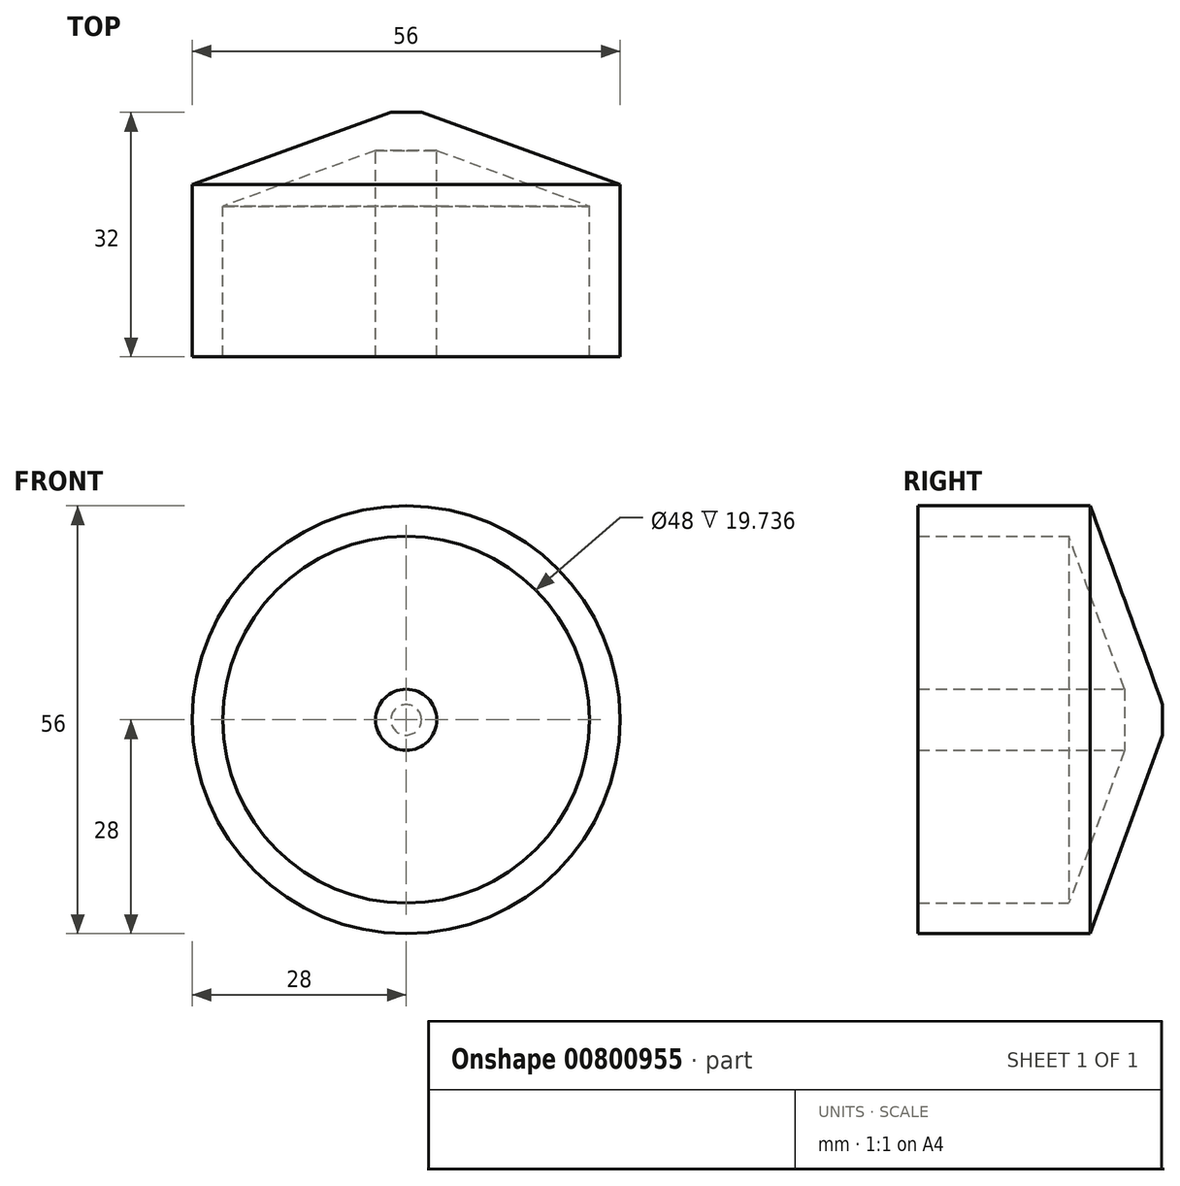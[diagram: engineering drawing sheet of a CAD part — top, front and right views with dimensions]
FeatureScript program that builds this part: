
annotation { "Feature Type Name" : "Feature", "Feature Type Description" : "" }
export const myFeature = defineFeature(function(context is Context, id is Id, definition is map)
    precondition{}
    {
        {
            var Q0;
            Q0=qCreatedBy(makeId("Top.planeOp"),FACE);
            var sketch = newSketch(context, id + "F0", { "sketchPlane" : qUnion([Q0])});
            skLineSegment(sketch, "E0", {"start": v(0, 0) * mm, "end": v(0, -32) * mm});
            skLineSegment(sketch, "E1", {"start": v(0, -32) * mm, "end": v(4, -32) * mm});
            skLineSegment(sketch, "E2", {"start": v(4, -32) * mm, "end": v(4, -4.98) * mm});
            skLineSegment(sketch, "E3", {"start": v(4, -4.98) * mm, "end": v(24, -12.26) * mm});
            skLineSegment(sketch, "E4", {"start": v(24, -12.26) * mm, "end": v(24, -32) * mm});
            skLineSegment(sketch, "E5", {"start": v(24, -32) * mm, "end": v(28, -32) * mm});
            skLineSegment(sketch, "E6", {"start": v(28, -32) * mm, "end": v(28, -9.46) * mm});
            skLineSegment(sketch, "E7", {"start": v(28, -9.46) * mm, "end": v(2, 0) * mm});
            skLineSegment(sketch, "E8", {"start": v(2, 0) * mm, "end": v(0, 0) * mm});
            skLineSegment(sketch, "E9", {"start": v(4, -32) * mm, "end": v(24, -32) * mm, "construction": true});
            skSolve(sketch);
        }
        {
            var Q0;
            Q0=makeQuery(id+"F0.imprint","IMPRINT",FACE,{"disambiguationData":[TD([[makeQuery(id+"F0.imprint","IMPRINT",EDGE,{"derivedFrom":sQuery(id+"F0.wireOp",EDGE,"E0")}),1.0]])]});
            var Q1;
            Q1=sQuery(id+"F0.wireOp",EDGE,"E0");
            revolve(context, id + "F1", {"surfaceOperationType" : NewSurfaceOperationType.NEW, "entities" : qUnion([Q0]), "axis" : qUnion([Q1]), "revolveType" : RevolveType.FULL});
        }
    });
